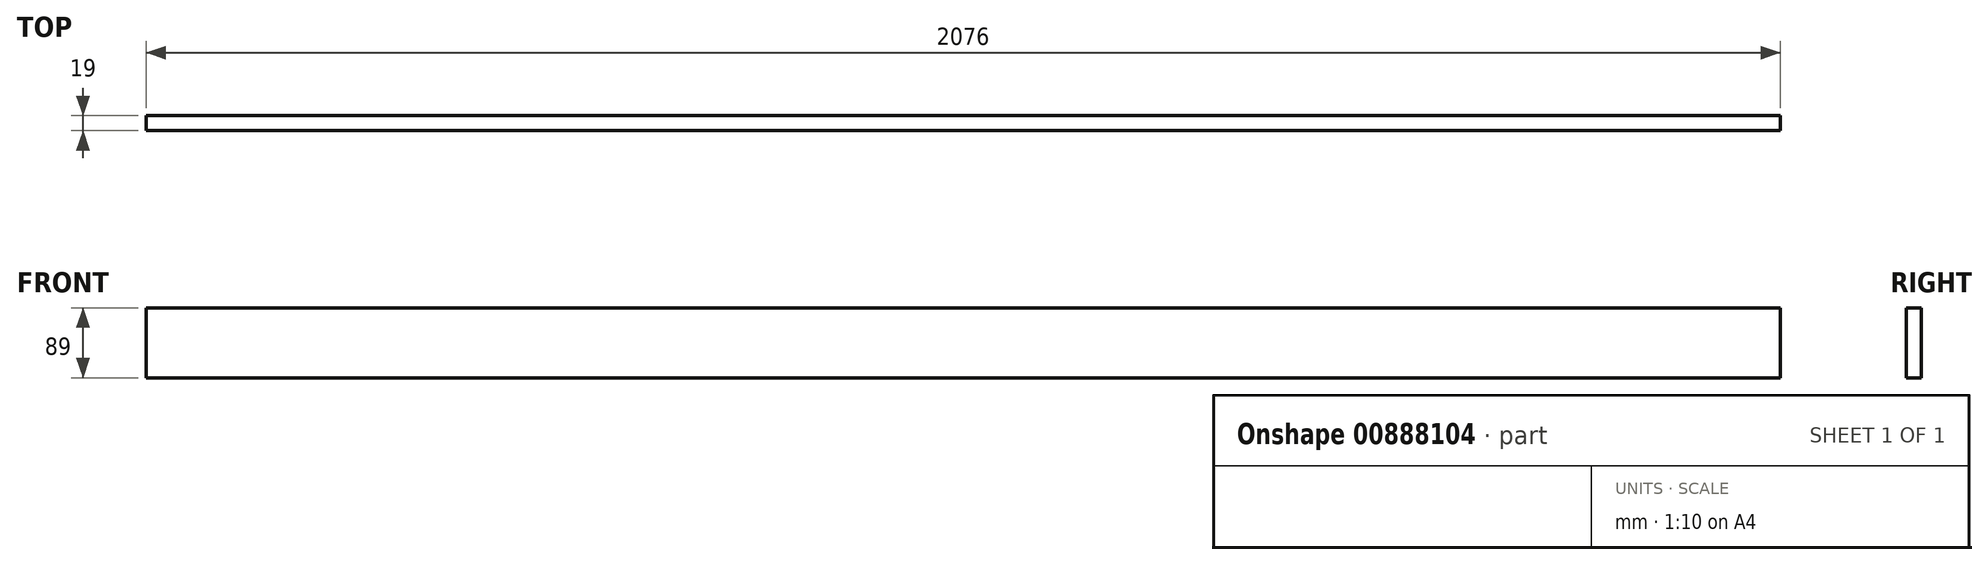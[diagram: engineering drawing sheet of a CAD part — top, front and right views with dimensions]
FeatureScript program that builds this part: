
annotation { "Feature Type Name" : "Feature", "Feature Type Description" : "" }
export const myFeature = defineFeature(function(context is Context, id is Id, definition is map)
    precondition{}
    {
        {
            var Q0;
            Q0=qCreatedBy(makeId("Front.planeOp"),FACE);
            var sketch = newSketch(context, id + "F0", { "sketchPlane" : qUnion([Q0])});
            skLineSegment(sketch, "E0.bottom", {"start": v(-1058.11, 89) * mm, "end": v(1017.89, 89) * mm});
            skLineSegment(sketch, "E0.top", {"start": v(-1058.11, 0) * mm, "end": v(1017.89, 0) * mm});
            skLineSegment(sketch, "E0.left", {"start": v(-1058.11, 89) * mm, "end": v(-1058.11, 0) * mm});
            skLineSegment(sketch, "E0.right", {"start": v(1017.89, 89) * mm, "end": v(1017.89, 0) * mm});
            skSolve(sketch);
        }
        {
            var Q0;
            Q0=makeQuery(id+"F0.imprint","IMPRINT",FACE,{"disambiguationData":[TD([[makeQuery(id+"F0.imprint","IMPRINT",EDGE,{"derivedFrom":sQuery(id+"F0.wireOp",EDGE,"E0.bottom")}),-1.0]])]});
            extrude(context, id + "F1", {"entities" : qUnion([Q0]), "depth" : 19 * mm, "offsetDistance" : 25 * mm});
        }
    });
